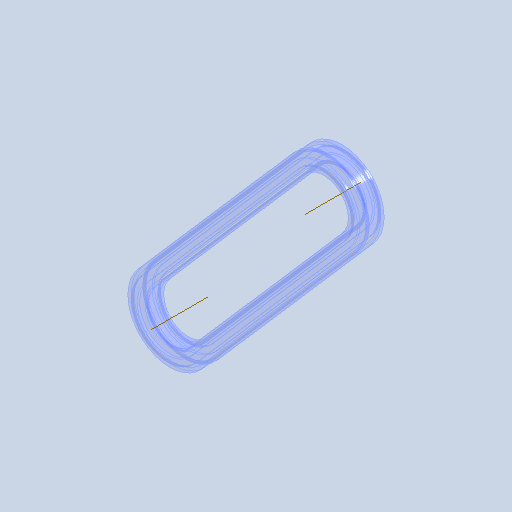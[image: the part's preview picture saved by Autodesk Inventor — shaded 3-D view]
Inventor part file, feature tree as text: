
AUTODESK INVENTOR PART (.ipt)
format: ipt  version: 2022.1 (Build 261234000, 234)  size: 169,984 bytes
history: native  units: mm
features: other x4, plane x2, sweep x1, pattern_linear x1, sketch x1
ambient origin geometry x8: Origin, YZ Plane, XZ Plane, XY Plane, X Axis, Y Axis, Z Axis, Center Point
bodies: Solid1 (feature_tree)
feature tree (9):
  other  "Eje de trabajo1"
  other  "Eje de trabajo2"
  plane  "Plano de trabajo2"
  plane  "Plano de trabajo3"
  other  "Trayectoria"
  other  "Plano de sección"
  sweep  "Sólido"
  pattern_linear  "Strand Pattern"  Spacing1=5.08mm  [1 undecoded]
  sketch  "Boceto de sección"  dims[d2=0.0mm d4=0.0mm d21=5.08mm d22=10.16mm d23=9.65mm d24=3.0mm d28=10.0mm d30=16.59mm d31=14.73mm d32=19.6mm d33=0.0mm d34=0.0mm d35=0.0mm d36=0.0mm d37=0.0mm]
note: 1 required parameter value undecoded (feature->parameter linkage not recoverable at this tier; creation-order binding heuristic only, values carry confidence <= 0.55)
